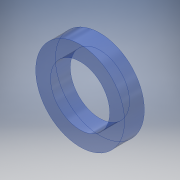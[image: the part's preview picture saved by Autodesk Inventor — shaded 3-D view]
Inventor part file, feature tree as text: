
AUTODESK INVENTOR PART (.ipt)
format: ipt  version: 2019.4 (Build 234330000, 330)  size: 105,472 bytes
history: native  units: mm
features: extrude x1, sketch x1
ambient origin geometry x8: Origin, YZ Plane, XZ Plane, XY Plane, X Axis, Y Axis, Z Axis, Center Point
bodies: Solid1 (feature_tree)
feature tree (2):
  extrude  "Extrusion1"  Depth=4.0mm
  sketch  "Sketch1"  dims[d0=18.0mm d1=12.0mm d2=4.0mm d3=0.0mm]
